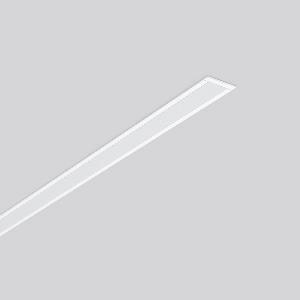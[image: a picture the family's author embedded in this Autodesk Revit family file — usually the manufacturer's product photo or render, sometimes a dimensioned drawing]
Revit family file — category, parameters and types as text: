
# Revit family: less_is_more_27_312176_002_8375
name_source: partatom
category: Lighting Fixtures
units: mm (PartAtom-declared; Revit-internal decimal feet)

## family parameters
Cut with Voids When Loaded = No
Host = Face
Light Source = No
Part Type = Normal
Room Calculation Point = No
Round Connector Dimension = Use Diameter
Shared = No

## types (1)
- LESS IS MORE 27 (1 x LED Modul 830, 1950 lm, 3000)
    Apparent Load = 29 VA
    CIE Flux Codes = 48 79 96 100 100
    Color Rendering = 80
    Color Temperature = 3000
    Default Elevation = 1800 mm
    Description = Series: LESS IS MORE 27
Recessed ceiling and wall luminaire with slim design. Housing: extruded aluminium profile, powder-coated. End cap aluminium powder-coated. Diffuser made of non-yellowing plastic (PMMA), opal. Suitable for Recessed ceiling mounting, wall (recessed). External driver with connecting cable. 
Colour: traffic white, matt (RAL 9016)
Length: 1014 mm
Width: 38 mm
Height: 2 mm
Cut-out length: 1006 mm
Cut-out width: 30 mm
Recess height: 45-60 mm
Luminaire: recess height: 37 mm
Lamp: LED
Socket: without socket
Colour temperature: 3000K
Colour rendering index (CRI): 82
System power: 29 W
Rated luminous flux: 1950 lm
Luminous efficiency: 67 lm/W
Control gear: Regulated power supply
Protection class: II
Type of protection: IP 20
    Height = 0 mm  [stored 0 ft]
    Lamp = 1 x LED Modul 830
    Lamp Light Flux = 1950 lm
    Lamp count = 1
    Length = 1014 mm
    Lifetime = 50000 h
    Luminous efficacy = 67 lm/W
    Manufacturer = RZB
    ModVariant = No
    Model = 312176.002
    Mounting Place = Ceiling, Wall
    Mounting Type = Recessed
    Number of Poles = 1
    OnlyDefault = Yes
    Power Factor = 1
    Product Name = LESS IS MORE 27
    Product group = Recessed LED linear luminaires
    ProductGroupID = 407
    Protection Class = Protection class II
    Protection Degree = IP 20
    RLX_Detail_Level = 1
    RLX_Emergency_Light_Flux = 0 lm
    RLX_Emergency_Type = 0
    RLX_Emergency_Type_DB = No
    RlxData = <blob elided: 21533 chars, md5=2758ab3a>
    Socket = socket
    Standby Power = 0 W
    System Light Flux = 1950 lm
    System Power = 29 W
    Type Comments = Product without accessories
    Type Image = 312176.002.jpg
    URL = http://relux.com
    VarID = ---
    Voltage = 230 V
    Voltage Range = 220-240 V
    Weight = 0.00 kg
    Width = 38 mm

note: [stored X ft] marks values corroborated as IEEE doubles in the binary element streams (Revit-internal decimal feet)

## geometry (parser evidence)
native form markers: Blend x4, Sweep x11
no freeform markers — native parametric forms only
